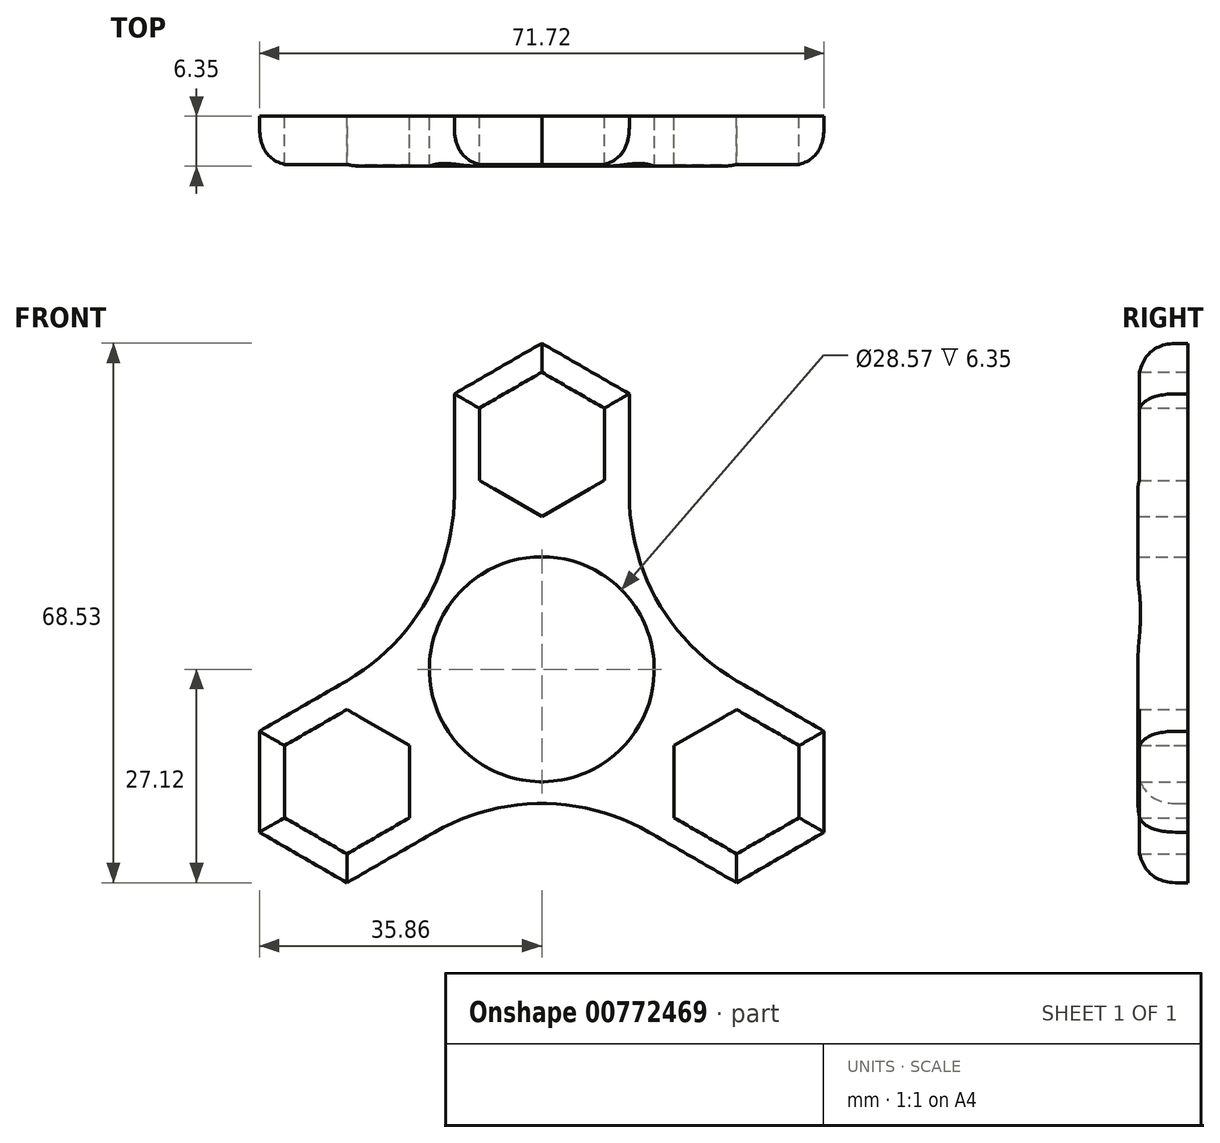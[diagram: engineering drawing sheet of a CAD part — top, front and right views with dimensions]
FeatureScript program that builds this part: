
annotation { "Feature Type Name" : "Feature", "Feature Type Description" : "" }
export const myFeature = defineFeature(function(context is Context, id is Id, definition is map)
    precondition{}
    {
        {
            var Q0;
            Q0=qCreatedBy(makeId("Front.planeOp"),FACE);
            var sketch = newSketch(context, id + "F0", { "sketchPlane" : qUnion([Q0])});
            skCircle(sketch, "E0", {"center": v(0, 0) * mm, "radius": 11.02 * mm});
            skCircle(sketch, "E1", {"center": v(0, 0) * mm, "radius": 14.29 * mm});
            skCircle(sketch, "E2.cCircle", {"center": v(0, 28.58) * mm, "radius": 7.94 * mm, "construction": true});
            skLineSegment(sketch, "E2.0", {"start": v(7.94, 33.16) * mm, "end": v(7.94, 24) * mm});
            skLineSegment(sketch, "E2.1", {"start": v(7.94, 24) * mm, "end": v(0, 19.4) * mm});
            skLineSegment(sketch, "E2.2", {"start": v(0, 19.4) * mm, "end": v(-7.94, 24) * mm});
            skLineSegment(sketch, "E2.3", {"start": v(-7.94, 24) * mm, "end": v(-7.94, 33.16) * mm});
            skLineSegment(sketch, "E2.4", {"start": v(-7.94, 33.16) * mm, "end": v(0, 37.74) * mm});
            skLineSegment(sketch, "E2.5", {"start": v(0, 37.74) * mm, "end": v(7.94, 33.16) * mm});
            skPoint(sketch, "E2.0.midPoint", {"position": v(7.94, 28.58) * mm});
            skCircle(sketch, "E3.cCircle", {"center": v(0, 28.58) * mm, "radius": 11.11 * mm, "construction": true});
            skLineSegment(sketch, "E3.0", {"start": v(11.11, 35) * mm, "end": v(11.11, 22.16) * mm});
            skLineSegment(sketch, "E3.1", {"start": v(11.11, 22.16) * mm, "end": v(0, 15.74) * mm});
            skLineSegment(sketch, "E3.2", {"start": v(0, 15.74) * mm, "end": v(-11.11, 22.16) * mm});
            skLineSegment(sketch, "E3.3", {"start": v(-11.11, 22.16) * mm, "end": v(-11.11, 35) * mm});
            skLineSegment(sketch, "E3.4", {"start": v(-11.11, 35) * mm, "end": v(0, 41.4) * mm});
            skLineSegment(sketch, "E3.5", {"start": v(0, 41.4) * mm, "end": v(11.11, 35) * mm});
            skPoint(sketch, "E3.0.midPoint", {"position": v(11.11, 28.58) * mm});
            skLineSegment(sketch, "E4.1.0", {"start": v(-24.75, -27.12) * mm, "end": v(-35.86, -20.7) * mm});
            skLineSegment(sketch, "E4.1.1", {"start": v(-13.63, -20.7) * mm, "end": v(-24.75, -27.12) * mm});
            skCircle(sketch, "E4.1.2", {"center": v(-24.75, -14.29) * mm, "radius": 11.11 * mm, "construction": true});
            skPoint(sketch, "E4.1.3", {"position": v(-30.3, -4.66) * mm});
            skLineSegment(sketch, "E4.1.4", {"start": v(-32.68, -18.87) * mm, "end": v(-32.68, -9.7) * mm});
            skLineSegment(sketch, "E4.1.5", {"start": v(-24.75, -23.45) * mm, "end": v(-32.68, -18.87) * mm});
            skLineSegment(sketch, "E4.1.6", {"start": v(-24.75, -1.46) * mm, "end": v(-13.63, -7.87) * mm});
            skLineSegment(sketch, "E4.1.7", {"start": v(-16.8, -18.87) * mm, "end": v(-24.75, -23.45) * mm});
            skLineSegment(sketch, "E4.1.8", {"start": v(-35.86, -20.7) * mm, "end": v(-35.86, -7.87) * mm});
            skPoint(sketch, "E4.1.11", {"position": v(-28.72, -7.41) * mm});
            skCircle(sketch, "E4.1.12", {"center": v(-24.75, -14.29) * mm, "radius": 7.94 * mm, "construction": true});
            skLineSegment(sketch, "E4.1.13", {"start": v(-13.63, -7.87) * mm, "end": v(-13.63, -20.7) * mm});
            skLineSegment(sketch, "E4.1.14", {"start": v(-35.86, -7.87) * mm, "end": v(-24.75, -1.46) * mm});
            skLineSegment(sketch, "E4.1.15", {"start": v(-32.68, -9.7) * mm, "end": v(-24.75, -5.12) * mm});
            skLineSegment(sketch, "E4.1.16", {"start": v(-16.8, -9.7) * mm, "end": v(-16.8, -18.87) * mm});
            skLineSegment(sketch, "E4.1.17", {"start": v(-24.75, -5.12) * mm, "end": v(-16.8, -9.7) * mm});
            skLineSegment(sketch, "E4.2.0", {"start": v(35.86, -7.87) * mm, "end": v(35.86, -20.7) * mm});
            skLineSegment(sketch, "E4.2.1", {"start": v(24.75, -1.46) * mm, "end": v(35.86, -7.87) * mm});
            skCircle(sketch, "E4.2.2", {"center": v(24.75, -14.29) * mm, "radius": 11.11 * mm, "construction": true});
            skPoint(sketch, "E4.2.3", {"position": v(19.2, -23.91) * mm});
            skLineSegment(sketch, "E4.2.4", {"start": v(32.68, -18.87) * mm, "end": v(24.75, -23.45) * mm});
            skLineSegment(sketch, "E4.2.5", {"start": v(32.68, -9.7) * mm, "end": v(32.68, -18.87) * mm});
            skLineSegment(sketch, "E4.2.6", {"start": v(13.63, -20.7) * mm, "end": v(13.63, -7.87) * mm});
            skLineSegment(sketch, "E4.2.7", {"start": v(24.75, -5.12) * mm, "end": v(32.68, -9.7) * mm});
            skLineSegment(sketch, "E4.2.8", {"start": v(35.86, -20.7) * mm, "end": v(24.75, -27.12) * mm});
            skPoint(sketch, "E4.2.11", {"position": v(20.78, -21.16) * mm});
            skCircle(sketch, "E4.2.12", {"center": v(24.75, -14.29) * mm, "radius": 7.94 * mm, "construction": true});
            skLineSegment(sketch, "E4.2.13", {"start": v(13.63, -7.87) * mm, "end": v(24.75, -1.46) * mm});
            skLineSegment(sketch, "E4.2.14", {"start": v(24.75, -27.12) * mm, "end": v(13.63, -20.7) * mm});
            skLineSegment(sketch, "E4.2.15", {"start": v(24.75, -23.45) * mm, "end": v(16.8, -18.87) * mm});
            skLineSegment(sketch, "E4.2.16", {"start": v(16.8, -9.7) * mm, "end": v(24.75, -5.12) * mm});
            skLineSegment(sketch, "E4.2.17", {"start": v(16.8, -18.87) * mm, "end": v(16.8, -9.7) * mm});
            skArc(sketch, "E5", {"start": v(-24.75, -1.46) * mm, "mid": v(-14.77, 8.53) * mm, "end": v(-11.11, 22.16) * mm});
            skArc(sketch, "E6", {"start": v(13.63, -20.7) * mm, "mid": v(0, -17.05) * mm, "end": v(-13.63, -20.7) * mm});
            skArc(sketch, "E7", {"start": v(11.11, 22.16) * mm, "mid": v(14.77, 8.53) * mm, "end": v(24.75, -1.46) * mm});
            skSolve(sketch);
        }
        {
            var Q0;
            Q0 = qSketchRegion(id + "F0", true);
            extrude(context, id + "F1", {"entities" : qUnion([Q0]), "depth" : 6.35 * mm, "offsetDistance" : 25.4 * mm});
        }
        {
            var Q0;
            Q0=makeQuery(id+"F1.opExtrude","CAP_EDGE",EDGE,{"disambiguationData":[OSD([sQuery(id+"F0.wireOp",EDGE,"E4.2.1")])],"isStart":false});
            var Q1;
            Q1=makeQuery(id+"F1.opExtrude","CAP_EDGE",EDGE,{"disambiguationData":[OSD([sQuery(id+"F0.wireOp",EDGE,"E4.2.0")])],"isStart":false});
            var Q2;
            Q2=makeQuery(id+"F1.opExtrude","CAP_EDGE",EDGE,{"disambiguationData":[OSD([sQuery(id+"F0.wireOp",EDGE,"E4.2.8")])],"isStart":false});
            var Q3;
            Q3=makeQuery(id+"F1.opExtrude","CAP_EDGE",EDGE,{"disambiguationData":[OSD([sQuery(id+"F0.wireOp",EDGE,"E4.2.14")])],"isStart":false});
            var Q4;
            Q4=makeQuery(id+"F1.opExtrude","CAP_EDGE",EDGE,{"disambiguationData":[OSD([sQuery(id+"F0.wireOp",EDGE,"E4.1.0")])],"isStart":false});
            var Q5;
            Q5=makeQuery(id+"F1.opExtrude","CAP_EDGE",EDGE,{"disambiguationData":[OSD([sQuery(id+"F0.wireOp",EDGE,"E4.1.8")])],"isStart":false});
            var Q6;
            Q6=makeQuery(id+"F1.opExtrude","CAP_EDGE",EDGE,{"disambiguationData":[OSD([sQuery(id+"F0.wireOp",EDGE,"E5")])],"isStart":false});
            var Q7;
            Q7=makeQuery(id+"F1.opExtrude","CAP_EDGE",EDGE,{"disambiguationData":[OSD([sQuery(id+"F0.wireOp",EDGE,"E4.1.14")])],"isStart":false});
            var Q8;
            Q8=makeQuery(id+"F1.opExtrude","CAP_EDGE",EDGE,{"disambiguationData":[OSD([sQuery(id+"F0.wireOp",EDGE,"E3.4")])],"isStart":false});
            var Q9;
            Q9=makeQuery(id+"F1.opExtrude","CAP_EDGE",EDGE,{"disambiguationData":[OSD([sQuery(id+"F0.wireOp",EDGE,"E3.5")])],"isStart":false});
            fillet(context, id + "F2", {"entities" : qUnion([Q0, Q1, Q2, Q3, Q4, Q5, Q6, Q7, Q8, Q9]), "radius" : 5.08 * mm, "tangentPropagation" : true, "rho" : 0.5, "crossSection" : FilletCrossSection.CONIC, "allowEdgeOverflow" : false});
        }
    });
